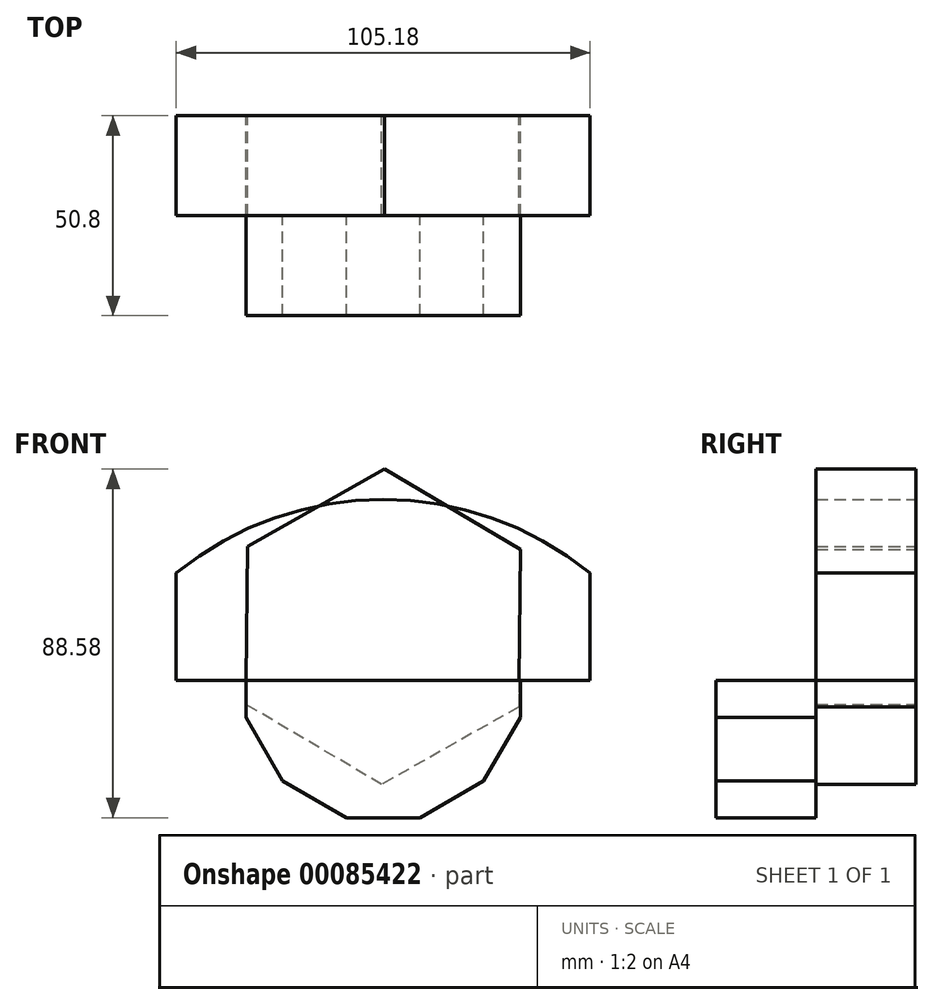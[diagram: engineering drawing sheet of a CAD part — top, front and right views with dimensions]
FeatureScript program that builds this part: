
annotation { "Feature Type Name" : "Feature", "Feature Type Description" : "" }
export const myFeature = defineFeature(function(context is Context, id is Id, definition is map)
    precondition{}
    {
        {
            var Q0;
            Q0=qCreatedBy(makeId("Front.planeOp"),FACE);
            var sketch = newSketch(context, id + "F0", { "sketchPlane" : qUnion([Q0])});
            skLineSegment(sketch, "E0.bottom", {"start": v(52.59, 13.66) * mm, "end": v(-52.59, 13.66) * mm});
            skLineSegment(sketch, "E0.top", {"start": v(52.59, -13.66) * mm, "end": v(-52.59, -13.66) * mm});
            skLineSegment(sketch, "E0.left", {"start": v(52.59, 13.66) * mm, "end": v(52.59, -13.66) * mm});
            skLineSegment(sketch, "E0.right", {"start": v(-52.59, 13.66) * mm, "end": v(-52.59, -13.66) * mm});
            skPoint(sketch, "E0.middle", {"position": v(0, 0) * mm});
            skArc(sketch, "E1", {"start": v(52.59, 13.66) * mm, "mid": v(0, 32.34) * mm, "end": v(-52.59, 13.66) * mm});
            skSolve(sketch);
        }
        {
            var Q0;
            Q0 = qSketchRegion(id + "F0", true);
            extrude(context, id + "F1", {"entities" : qUnion([Q0]), "depth" : 25.4 * mm});
        }
        {
            var Q0;
            Q0=makeQuery(id+"F1.opExtrude","CAP_FACE",FACE,{"disambiguationData":[OSD([sQuery(id+"F0.wireOp",EDGE,"E0.top"),sQuery(id+"F0.wireOp",EDGE,"E0.left"),sQuery(id+"F0.wireOp",EDGE,"E0.right"),sQuery(id+"F0.wireOp",EDGE,"E1")])],"isStart":false});
            var sketch = newSketch(context, id + "F2", { "sketchPlane" : qUnion([Q0])});
            skCircle(sketch, "E2.cCircle", {"center": v(0, -13.66) * mm, "radius": 34.87 * mm, "construction": true});
            skPoint(sketch, "E2.cCircle.perimeterSnap0", {"position": v(0, -13.66) * mm});
            skLineSegment(sketch, "E2.0", {"start": v(9.34, -48.53) * mm, "end": v(-9.34, -48.53) * mm});
            skLineSegment(sketch, "E2.1", {"start": v(-9.34, -48.53) * mm, "end": v(-25.53, -39.2) * mm});
            skLineSegment(sketch, "E2.2", {"start": v(-25.53, -39.2) * mm, "end": v(-34.87, -23) * mm});
            skLineSegment(sketch, "E2.3", {"start": v(-34.87, -23) * mm, "end": v(-34.87, -4.32) * mm});
            skLineSegment(sketch, "E2.4", {"start": v(-34.87, -4.32) * mm, "end": v(-25.53, 11.86) * mm});
            skLineSegment(sketch, "E2.5", {"start": v(-25.53, 11.86) * mm, "end": v(-9.34, 21.2) * mm});
            skLineSegment(sketch, "E2.6", {"start": v(-9.34, 21.2) * mm, "end": v(9.34, 21.2) * mm});
            skLineSegment(sketch, "E2.7", {"start": v(9.34, 21.2) * mm, "end": v(25.53, 11.86) * mm});
            skLineSegment(sketch, "E2.8", {"start": v(25.53, 11.86) * mm, "end": v(34.87, -4.32) * mm});
            skLineSegment(sketch, "E2.9", {"start": v(34.87, -4.32) * mm, "end": v(34.87, -23) * mm});
            skLineSegment(sketch, "E2.10", {"start": v(34.87, -23) * mm, "end": v(25.53, -39.2) * mm});
            skLineSegment(sketch, "E2.11", {"start": v(25.53, -39.2) * mm, "end": v(9.34, -48.53) * mm});
            skPoint(sketch, "E2.0.midPoint", {"position": v(0, -48.53) * mm});
            skPoint(sketch, "E2.0.midPoint.positionSnap0", {"position": v(0, -13.66) * mm});
            skSolve(sketch);
        }
        {
            var Q0;
            Q0=makeQuery(id+"F2.imprint","IMPRINT",FACE,{"disambiguationData":[TD([[makeQuery(id+"F2.imprint","IMPRINT",EDGE,{"derivedFrom":sQuery(id+"F2.wireOp",EDGE,"E2.0")}),-1.0]])]});
            extrude(context, id + "F3", {"entities" : qUnion([Q0]), "depth" : 25.4 * mm});
        }
        {
            var Q0;
            Q0=qCreatedBy(makeId("Front.planeOp"),FACE);
            var sketch = newSketch(context, id + "F4", { "sketchPlane" : qUnion([Q0])});
            skCircle(sketch, "E3.cCircle", {"center": v(0, 0) * mm, "radius": 40.05 * mm, "construction": true});
            skLineSegment(sketch, "E3.0", {"start": v(-34.87, -19.7) * mm, "end": v(-34.5, 20.35) * mm});
            skLineSegment(sketch, "E3.1", {"start": v(-34.5, 20.35) * mm, "end": v(0.38, 40.05) * mm});
            skLineSegment(sketch, "E3.2", {"start": v(0.38, 40.05) * mm, "end": v(34.87, 19.7) * mm});
            skLineSegment(sketch, "E3.3", {"start": v(34.87, 19.7) * mm, "end": v(34.5, -20.35) * mm});
            skLineSegment(sketch, "E3.4", {"start": v(34.5, -20.35) * mm, "end": v(-0.38, -40.05) * mm});
            skLineSegment(sketch, "E3.5", {"start": v(-0.38, -40.05) * mm, "end": v(-34.87, -19.7) * mm});
            skSolve(sketch);
        }
        {
            var Q0;
            Q0 = qSketchRegion(id + "F4", true);
            extrude(context, id + "F5", {"entities" : qUnion([Q0]), "depth" : 25.4 * mm});
        }
    });
